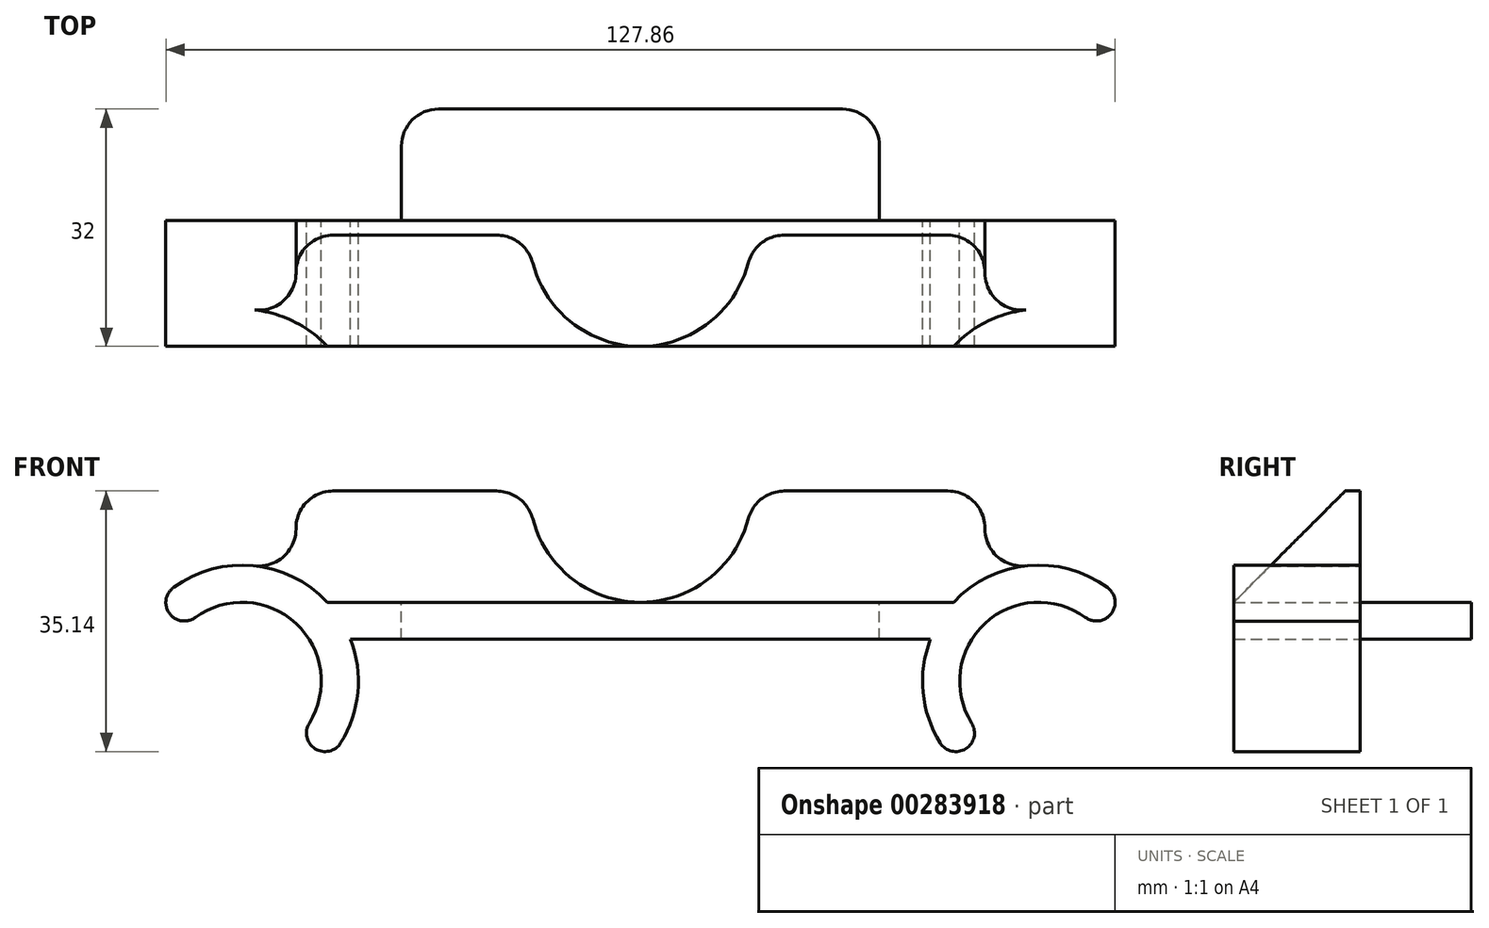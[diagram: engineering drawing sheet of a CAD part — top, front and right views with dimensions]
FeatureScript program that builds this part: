
annotation { "Feature Type Name" : "Feature", "Feature Type Description" : "" }
export const myFeature = defineFeature(function(context is Context, id is Id, definition is map)
    precondition{}
    {
        {
            var Q0;
            Q0=qCreatedBy(makeId("Front.planeOp"),FACE);
            var sketch = newSketch(context, id + "F0", { "sketchPlane" : qUnion([Q0])});
            skLineSegment(sketch, "E0", {"start": v(0, 0) * mm, "end": v(0, 38.7) * mm, "construction": true});
            skLineSegment(sketch, "E1", {"start": v(-43, 0) * mm, "end": v(43, 0) * mm, "construction": true});
            skCircle(sketch, "E2", {"center": v(53.67, 0) * mm, "radius": 10.67 * mm, "construction": true});
            skCircle(sketch, "E3", {"center": v(53.67, 0) * mm, "radius": 15.67 * mm, "construction": true});
            skLineSegment(sketch, "E4", {"start": v(53.67, 0) * mm, "end": v(53.67, 10.67) * mm, "construction": true});
            skLineSegment(sketch, "E5", {"start": v(53.67, 10.67) * mm, "end": v(0, 10.67) * mm, "construction": true});
            skArc(sketch, "E6", {"start": v(42.2, -10.67) * mm, "mid": v(38.28, -2.95) * mm, "end": v(39.06, 5.67) * mm});
            skArc(sketch, "E7", {"start": v(45.85, -7.26) * mm, "mid": v(46.4, 7.81) * mm, "end": v(61.48, 7.26) * mm});
            skLineSegment(sketch, "E8", {"start": v(53.67, 0) * mm, "end": v(53.67, -10.67) * mm, "construction": true});
            skLineSegment(sketch, "E9", {"start": v(42.2, -10.67) * mm, "end": v(65.14, 10.67) * mm, "construction": true});
            skLineSegment(sketch, "E10", {"start": v(42.2, -10.67) * mm, "end": v(45.85, -7.26) * mm});
            skLineSegment(sketch, "E11", {"start": v(61.48, 7.26) * mm, "end": v(65.14, 10.67) * mm});
            skArc(sketch, "E12", {"start": v(42.2, 10.67) * mm, "mid": v(53.67, 15.67) * mm, "end": v(65.14, 10.67) * mm});
            skLineSegment(sketch, "E13.MirrorCS", {"start": v(-42.2, -10.67) * mm, "end": v(-45.85, -7.26) * mm});
            skLineSegment(sketch, "E14.MirrorCS", {"start": v(-61.48, 7.26) * mm, "end": v(-65.14, 10.67) * mm});
            skArc(sketch, "E15.MirrorCS", {"start": v(-45.85, -7.26) * mm, "mid": v(-46.4, 7.81) * mm, "end": v(-61.48, 7.26) * mm});
            skArc(sketch, "E16.MirrorCS", {"start": v(-42.2, 10.67) * mm, "mid": v(-53.67, 15.67) * mm, "end": v(-65.14, 10.67) * mm});
            skArc(sketch, "E17.MirrorCS", {"start": v(-42.2, -10.67) * mm, "mid": v(-38.28, -2.95) * mm, "end": v(-39.06, 5.67) * mm});
            skLineSegment(sketch, "E18", {"start": v(-42.2, 10.67) * mm, "end": v(42.2, 10.67) * mm});
            skLineSegment(sketch, "E19", {"start": v(-39.06, 5.67) * mm, "end": v(39.06, 5.67) * mm});
            skSolve(sketch);
        }
        {
            var Q0;
            Q0=qSketchRegion(id+"F0",true);
            extrude(context, id + "F1", {"entities" : qUnion([Q0]), "depth" : 17 * mm});
        }
        {
            var Q0;
            Q0=makeQuery(id+"F1.opExtrude","CAP_FACE",FACE,{"disambiguationData":[OSD([sQuery(id+"F0.wireOp",EDGE,"E6"),sQuery(id+"F0.wireOp",EDGE,"E7"),sQuery(id+"F0.wireOp",EDGE,"E10"),sQuery(id+"F0.wireOp",EDGE,"E11"),sQuery(id+"F0.wireOp",EDGE,"E12"),sQuery(id+"F0.wireOp",EDGE,"E13.MirrorCS"),sQuery(id+"F0.wireOp",EDGE,"E14.MirrorCS"),sQuery(id+"F0.wireOp",EDGE,"E15.MirrorCS"),sQuery(id+"F0.wireOp",EDGE,"E16.MirrorCS"),sQuery(id+"F0.wireOp",EDGE,"E17.MirrorCS"),sQuery(id+"F0.wireOp",EDGE,"E18"),sQuery(id+"F0.wireOp",EDGE,"E19")])],"isStart":true});
            var sketch = newSketch(context, id + "F2", { "sketchPlane" : qUnion([Q0])});
            skLineSegment(sketch, "E20.bottom", {"start": v(-46.4, 7.81) * mm, "end": v(46.4, 7.81) * mm});
            skLineSegment(sketch, "E20.top", {"start": v(-46.4, 25.67) * mm, "end": v(46.4, 25.67) * mm});
            skLineSegment(sketch, "E20.left", {"start": v(-46.4, 7.81) * mm, "end": v(-46.4, 25.67) * mm});
            skLineSegment(sketch, "E20.right", {"start": v(46.4, 7.81) * mm, "end": v(46.4, 25.67) * mm});
            skSolve(sketch);
        }
        {
            var Q0;
            Q0=qSketchRegion(id+"F2",true);
            extrude(context, id + "F3", {"entities" : qUnion([Q0]), "operationType" : NewBodyOperationType.ADD, "oppositeDirection" : true, "depth" : 2 * mm});
        }
        {
            var Q0;
            Q0=makeQuery(id+"F3.boolean.opBoolean","MERGE",FACE,{"derivedFrom":[makeQuery(id+"F1.opExtrude","CAP_FACE",FACE,{"disambiguationData":[OSD([sQuery(id+"F0.wireOp",EDGE,"E6"),sQuery(id+"F0.wireOp",EDGE,"E7"),sQuery(id+"F0.wireOp",EDGE,"E10"),sQuery(id+"F0.wireOp",EDGE,"E11"),sQuery(id+"F0.wireOp",EDGE,"E12"),sQuery(id+"F0.wireOp",EDGE,"E13.MirrorCS"),sQuery(id+"F0.wireOp",EDGE,"E14.MirrorCS"),sQuery(id+"F0.wireOp",EDGE,"E15.MirrorCS"),sQuery(id+"F0.wireOp",EDGE,"E16.MirrorCS"),sQuery(id+"F0.wireOp",EDGE,"E17.MirrorCS"),sQuery(id+"F0.wireOp",EDGE,"E18"),sQuery(id+"F0.wireOp",EDGE,"E19")])],"isStart":true}),makeQuery(id+"F3.opExtrude","CAP_FACE",FACE,{"disambiguationData":[OSD([sQuery(id+"F2.wireOp",EDGE,"E20.bottom"),sQuery(id+"F2.wireOp",EDGE,"E20.top"),sQuery(id+"F2.wireOp",EDGE,"E20.left"),sQuery(id+"F2.wireOp",EDGE,"E20.right")])],"isStart":true})]});
            var sketch = newSketch(context, id + "F4", { "sketchPlane" : qUnion([Q0])});
            skLineSegment(sketch, "E21.0", {"start": v(-42.2, 10.67) * mm, "end": v(42.2, 10.67) * mm, "construction": true});
            skLineSegment(sketch, "E22.bottom", {"start": v(-32.2, 5.67) * mm, "end": v(32.2, 5.67) * mm});
            skLineSegment(sketch, "E22.top", {"start": v(-32.2, 10.67) * mm, "end": v(32.2, 10.67) * mm});
            skLineSegment(sketch, "E22.left", {"start": v(-32.2, 5.67) * mm, "end": v(-32.2, 10.67) * mm});
            skLineSegment(sketch, "E22.right", {"start": v(32.2, 5.67) * mm, "end": v(32.2, 10.67) * mm});
            skSolve(sketch);
        }
        {
            var Q0;
            Q0=qSketchRegion(id+"F4",true);
            extrude(context, id + "F5", {"entities" : qUnion([Q0]), "operationType" : NewBodyOperationType.ADD, "depth" : 15 * mm});
        }
        {
            var Q0;
            Q0=makeQuery(id+"F1.opExtrude","SWEPT_EDGE",EDGE,{"disambiguationData":[OSD([sQuery(id+"F0.wireOp",EDGE,"E7"),sQuery(id+"F0.wireOp",EDGE,"E10")])]});
            var Q1;
            Q1=makeQuery(id+"F1.opExtrude","SWEPT_EDGE",EDGE,{"disambiguationData":[OSD([sQuery(id+"F0.wireOp",EDGE,"E6"),sQuery(id+"F0.wireOp",EDGE,"E10")])]});
            var Q2;
            Q2=makeQuery(id+"F1.opExtrude","SWEPT_EDGE",EDGE,{"disambiguationData":[OSD([sQuery(id+"F0.wireOp",EDGE,"E11"),sQuery(id+"F0.wireOp",EDGE,"E12")])]});
            var Q3;
            Q3=makeQuery(id+"F1.opExtrude","SWEPT_EDGE",EDGE,{"disambiguationData":[OSD([sQuery(id+"F0.wireOp",EDGE,"E7"),sQuery(id+"F0.wireOp",EDGE,"E11")])]});
            var Q4;
            Q4=makeQuery(id+"F1.opExtrude","SWEPT_EDGE",EDGE,{"disambiguationData":[OSD([sQuery(id+"F0.wireOp",EDGE,"E13.MirrorCS"),sQuery(id+"F0.wireOp",EDGE,"E17.MirrorCS")])]});
            var Q5;
            Q5=makeQuery(id+"F1.opExtrude","SWEPT_EDGE",EDGE,{"disambiguationData":[OSD([sQuery(id+"F0.wireOp",EDGE,"E13.MirrorCS"),sQuery(id+"F0.wireOp",EDGE,"E15.MirrorCS")])]});
            var Q6;
            Q6=makeQuery(id+"F1.opExtrude","SWEPT_EDGE",EDGE,{"disambiguationData":[OSD([sQuery(id+"F0.wireOp",EDGE,"E14.MirrorCS"),sQuery(id+"F0.wireOp",EDGE,"E15.MirrorCS")])]});
            var Q7;
            Q7=makeQuery(id+"F1.opExtrude","SWEPT_EDGE",EDGE,{"disambiguationData":[OSD([sQuery(id+"F0.wireOp",EDGE,"E14.MirrorCS"),sQuery(id+"F0.wireOp",EDGE,"E16.MirrorCS")])]});
            fillet(context, id + "F6", {"entities" : qUnion([Q0, Q1, Q2, Q3, Q4, Q5, Q6, Q7]), "radius" : 2.5 * mm, "tangentPropagation" : true, "allowEdgeOverflow" : false});
        }
        {
            var Q0;
            Q0=makeQuery(id+"F3.opExtrude","SWEPT_EDGE",EDGE,{"disambiguationData":[OSD([sQuery(id+"F2.wireOp",EDGE,"E20.top"),sQuery(id+"F2.wireOp",EDGE,"E20.left")])]});
            var Q1;
            Q1=makeQuery(id+"F3.boolean.opBoolean","INTERSECT",EDGE,{"derivedFrom":[makeQuery(id+"F1.opExtrude","SWEPT_FACE",FACE,{"disambiguationData":[OSD([sQuery(id+"F0.wireOp",EDGE,"E12")])]}),makeQuery(id+"F3.opExtrude","SWEPT_FACE",FACE,{"disambiguationData":[OSD([sQuery(id+"F2.wireOp",EDGE,"E20.left")])]})]});
            var Q2;
            Q2=makeQuery(id+"F3.opExtrude","SWEPT_EDGE",EDGE,{"disambiguationData":[OSD([sQuery(id+"F2.wireOp",EDGE,"E20.top"),sQuery(id+"F2.wireOp",EDGE,"E20.right")])]});
            var Q3;
            Q3=makeQuery(id+"F3.boolean.opBoolean","INTERSECT",EDGE,{"derivedFrom":[makeQuery(id+"F1.opExtrude","SWEPT_FACE",FACE,{"disambiguationData":[OSD([sQuery(id+"F0.wireOp",EDGE,"E16.MirrorCS")])]}),makeQuery(id+"F3.opExtrude","SWEPT_FACE",FACE,{"disambiguationData":[OSD([sQuery(id+"F2.wireOp",EDGE,"E20.right")])]})]});
            var Q4;
            Q4=makeQuery(id+"F5.opExtrude","CAP_EDGE",EDGE,{"disambiguationData":[OSD([sQuery(id+"F4.wireOp",EDGE,"E22.right")])],"isStart":true});
            var Q5;
            Q5=makeQuery(id+"F5.opExtrude","CAP_EDGE",EDGE,{"disambiguationData":[OSD([sQuery(id+"F4.wireOp",EDGE,"E22.left")])],"isStart":true});
            var Q6;
            Q6=makeQuery(id+"F5.opExtrude","CAP_EDGE",EDGE,{"disambiguationData":[OSD([sQuery(id+"F4.wireOp",EDGE,"E22.left")])],"isStart":false});
            var Q7;
            Q7=makeQuery(id+"F5.opExtrude","CAP_EDGE",EDGE,{"disambiguationData":[OSD([sQuery(id+"F4.wireOp",EDGE,"E22.right")])],"isStart":false});
            fillet(context, id + "F7", {"entities" : qUnion([Q0, Q1, Q2, Q3, Q4, Q5, Q6, Q7]), "radius" : 5 * mm, "tangentPropagation" : true, "allowEdgeOverflow" : false});
        }
        {
            var Q0;
            Q0=makeQuery(id+"F3.boolean.opBoolean","INTERSECT",EDGE,{"derivedFrom":[makeQuery(id+"F1.opExtrude","SWEPT_FACE",FACE,{"disambiguationData":[OSD([sQuery(id+"F0.wireOp",EDGE,"E18")])]}),makeQuery(id+"F3.opExtrude","CAP_FACE",FACE,{"disambiguationData":[OSD([sQuery(id+"F2.wireOp",EDGE,"E20.bottom"),sQuery(id+"F2.wireOp",EDGE,"E20.top"),sQuery(id+"F2.wireOp",EDGE,"E20.left"),sQuery(id+"F2.wireOp",EDGE,"E20.right")])],"isStart":false})]});
            chamfer(context, id + "F8", {"entities" : qUnion([Q0]), "chamferType" : ChamferType.TWO_OFFSETS, "width1" : 15 * mm, "oppositeDirection" : false, "width2" : 15 * mm, "tangentPropagation" : true});
        }
        {
            var Q0;
            Q0=makeQuery(id+"F3.boolean.opBoolean","MERGE",FACE,{"derivedFrom":[makeQuery(id+"F1.opExtrude","CAP_FACE",FACE,{"disambiguationData":[OSD([sQuery(id+"F0.wireOp",EDGE,"E6"),sQuery(id+"F0.wireOp",EDGE,"E7"),sQuery(id+"F0.wireOp",EDGE,"E10"),sQuery(id+"F0.wireOp",EDGE,"E11"),sQuery(id+"F0.wireOp",EDGE,"E12"),sQuery(id+"F0.wireOp",EDGE,"E13.MirrorCS"),sQuery(id+"F0.wireOp",EDGE,"E14.MirrorCS"),sQuery(id+"F0.wireOp",EDGE,"E15.MirrorCS"),sQuery(id+"F0.wireOp",EDGE,"E16.MirrorCS"),sQuery(id+"F0.wireOp",EDGE,"E17.MirrorCS"),sQuery(id+"F0.wireOp",EDGE,"E18"),sQuery(id+"F0.wireOp",EDGE,"E19")])],"isStart":true}),makeQuery(id+"F3.opExtrude","CAP_FACE",FACE,{"disambiguationData":[OSD([sQuery(id+"F2.wireOp",EDGE,"E20.bottom"),sQuery(id+"F2.wireOp",EDGE,"E20.top"),sQuery(id+"F2.wireOp",EDGE,"E20.left"),sQuery(id+"F2.wireOp",EDGE,"E20.right")])],"isStart":true})]});
            var sketch = newSketch(context, id + "F9", { "sketchPlane" : qUnion([Q0])});
            skLineSegment(sketch, "E23", {"start": v(0, 10.67) * mm, "end": v(0, 25.67) * mm, "construction": true});
            skCircle(sketch, "E24", {"center": v(0, 25.67) * mm, "radius": 15 * mm});
            skSolve(sketch);
        }
        {
            var Q0;
            Q0 = qSketchRegion(id + "F9", true);
            extrude(context, id + "F10", {"entities" : qUnion([Q0]), "operationType" : NewBodyOperationType.REMOVE, "endBound" : BoundingType.THROUGH_ALL, "oppositeDirection" : true, "depth" : 25 * mm});
        }
        {
            var Q0;
            Q0=makeQuery(id+"F10.boolean.opBoolean","INTERSECT",EDGE,{"disambiguationData":[OD(0.0)],"derivedFrom":[makeQuery(id+"F3.opExtrude","SWEPT_FACE",FACE,{"disambiguationData":[OSD([sQuery(id+"F2.wireOp",EDGE,"E20.top")])]}),makeQuery(id+"F10.opExtrude","SWEPT_FACE",FACE,{"disambiguationData":[OSD([sQuery(id+"F9.wireOp",EDGE,"E24")])]})]});
            var Q1;
            Q1=makeQuery(id+"F10.boolean.opBoolean","INTERSECT",EDGE,{"disambiguationData":[OD(1.0)],"derivedFrom":[makeQuery(id+"F3.opExtrude","SWEPT_FACE",FACE,{"disambiguationData":[OSD([sQuery(id+"F2.wireOp",EDGE,"E20.top")])]}),makeQuery(id+"F10.opExtrude","SWEPT_FACE",FACE,{"disambiguationData":[OSD([sQuery(id+"F9.wireOp",EDGE,"E24")])]})]});
            fillet(context, id + "F11", {"entities" : qUnion([Q0, Q1]), "radius" : 5 * mm, "tangentPropagation" : true, "allowEdgeOverflow" : false});
        }
    });
